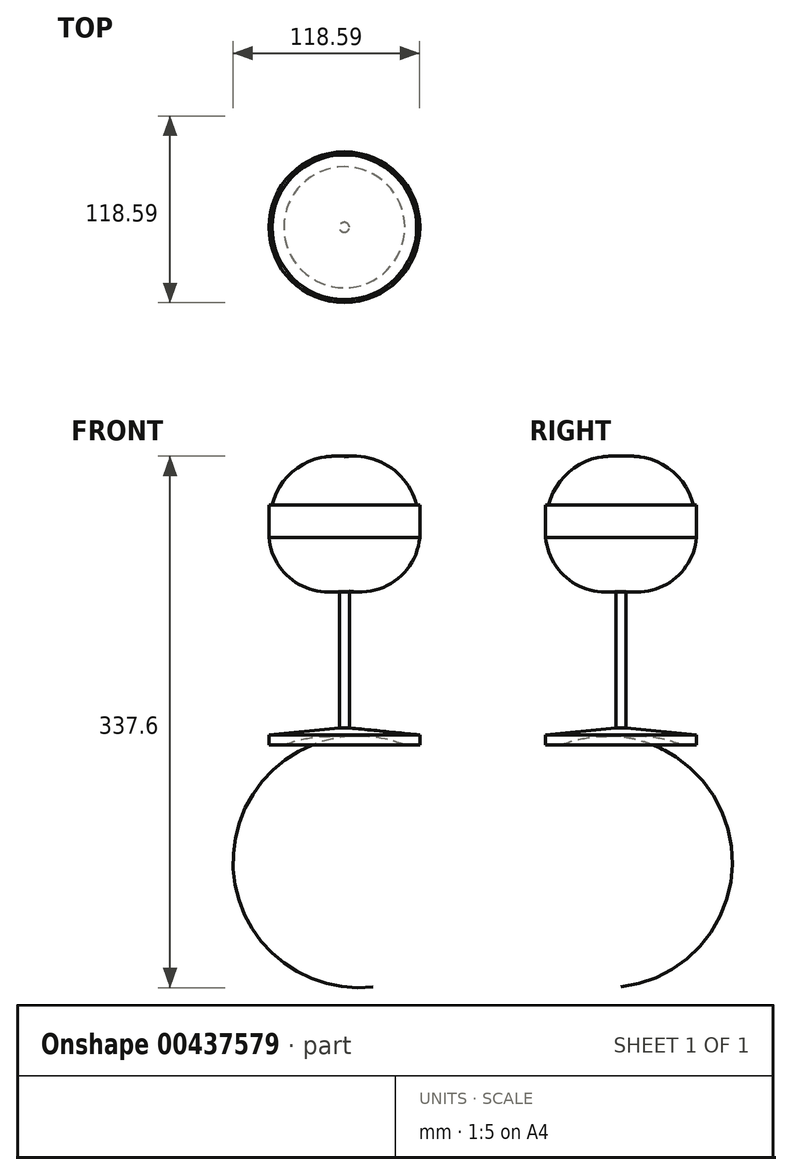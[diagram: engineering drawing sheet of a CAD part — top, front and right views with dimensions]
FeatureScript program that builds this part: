
annotation { "Feature Type Name" : "Feature", "Feature Type Description" : "" }
export const myFeature = defineFeature(function(context is Context, id is Id, definition is map)
    precondition{}
    {
        {
            var Q0;
            Q0=qCreatedBy(makeId("Front.planeOp"),FACE);
            var sketch = newSketch(context, id + "F0", { "sketchPlane" : qUnion([Q0])});
            skLineSegment(sketch, "E0", {"start": v(-38.4, 0) * mm, "end": v(-47.9, 0) * mm});
            skLineSegment(sketch, "E1", {"start": v(-47.9, 0) * mm, "end": v(-47.9, 6.35) * mm});
            skLineSegment(sketch, "E2", {"start": v(-47.9, 6.35) * mm, "end": v(-3.18, 10.85) * mm});
            skLineSegment(sketch, "E3", {"start": v(-3.18, 10.85) * mm, "end": v(-3.18, 97.78) * mm});
            skLineSegment(sketch, "E4", {"start": v(-47.9, 131.77) * mm, "end": v(-47.9, 152.4) * mm});
            skLineSegment(sketch, "E5", {"start": v(-47.9, 152.4) * mm, "end": v(-46, 152.4) * mm});
            skLineSegment(sketch, "E6", {"start": v(0, 101.9) * mm, "end": v(0, 5.02) * mm});
            skArc(sketch, "E7", {"start": v(-46, 152.4) * mm, "mid": v(-36.53, 114.82) * mm, "end": v(0, 101.9) * mm});
            skArc(sketch, "E8", {"start": v(-47.9, 131.77) * mm, "mid": v(-33.05, 104.89) * mm, "end": v(-3.17, 97.78) * mm});
            skArc(sketch, "E9", {"start": v(0, 5.02) * mm, "mid": v(-19.51, 4.87) * mm, "end": v(-38.4, 0) * mm});
            skSolve(sketch);
        }
        {
            var Q0;
            Q0=makeQuery(id+"F0.imprint","IMPRINT",FACE,{"disambiguationData":[TD([[makeQuery(id+"F0.imprint","IMPRINT",EDGE,{"derivedFrom":sQuery(id+"F0.wireOp",EDGE,"E0")}),-1.0]])]});
            var Q1;
            Q1=sQuery(id+"F0.wireOp",EDGE,"E6");
            revolve(context, id + "F1", {"entities" : qUnion([Q0]), "axis" : qUnion([Q1]), "revolveType" : RevolveType.FULL});
        }
    });
